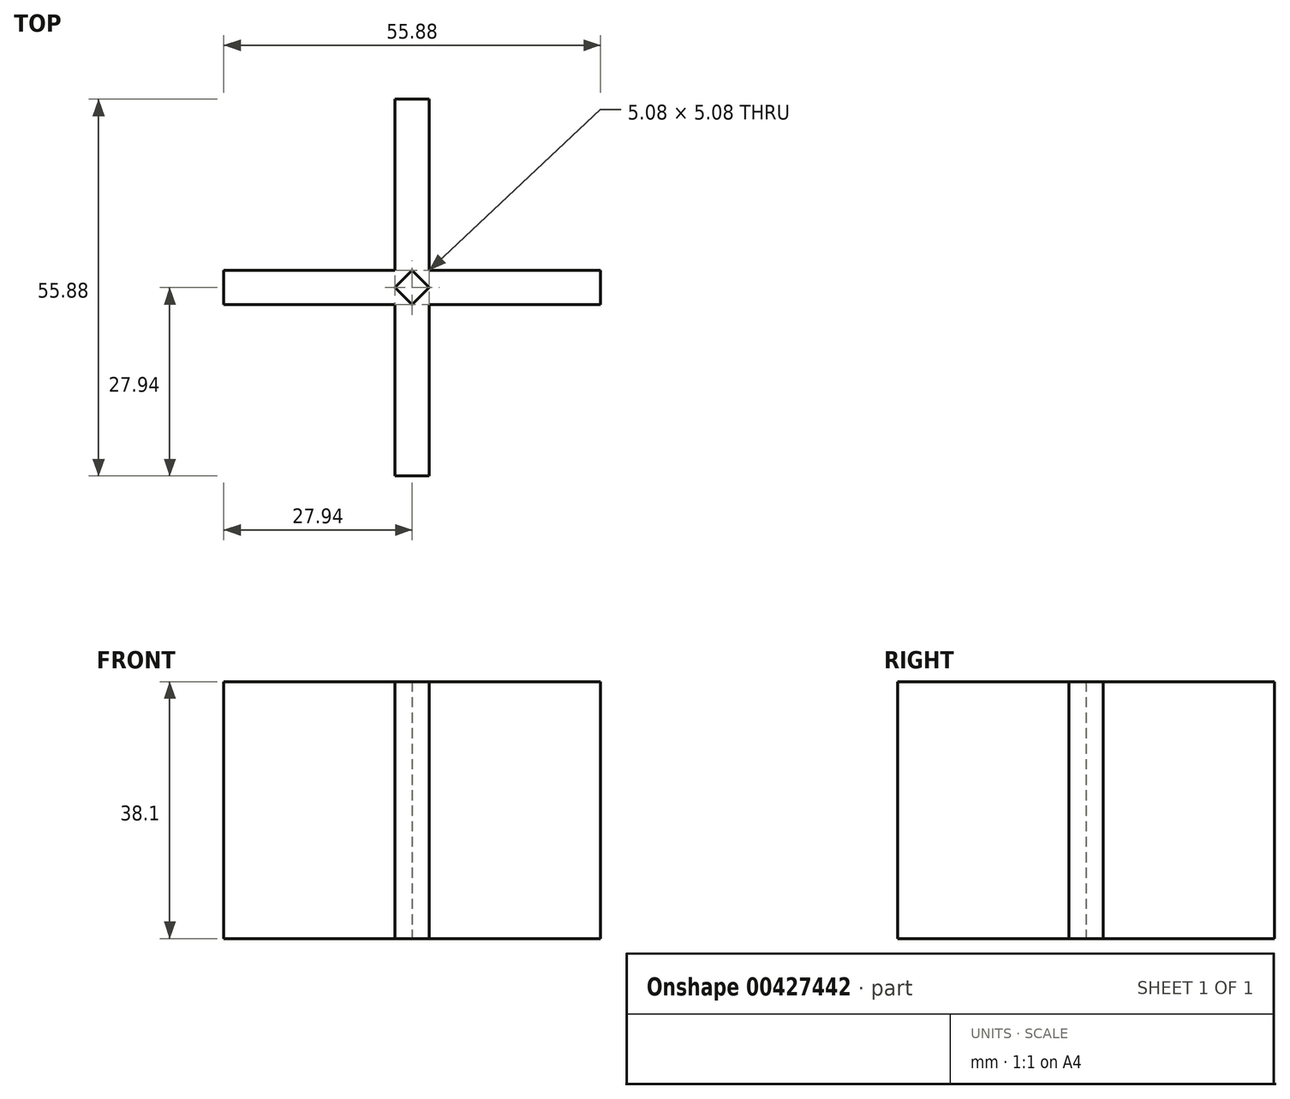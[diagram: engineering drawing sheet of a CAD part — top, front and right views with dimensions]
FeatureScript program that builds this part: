
annotation { "Feature Type Name" : "Feature", "Feature Type Description" : "" }
export const myFeature = defineFeature(function(context is Context, id is Id, definition is map)
    precondition{}
    {
        {
            var Q0;
            Q0=qCreatedBy(makeId("Top.planeOp"),FACE);
            var sketch = newSketch(context, id + "F0", { "sketchPlane" : qUnion([Q0])});
            skLineSegment(sketch, "E0", {"start": v(0, 0) * mm, "end": v(0, 25.4) * mm});
            skLineSegment(sketch, "E1", {"start": v(0, 25.4) * mm, "end": v(5.08, 25.4) * mm});
            skLineSegment(sketch, "E2", {"start": v(5.08, -30.48) * mm, "end": v(0, -30.48) * mm});
            skLineSegment(sketch, "E3", {"start": v(0, -30.48) * mm, "end": v(0, -5.08) * mm});
            skLineSegment(sketch, "E4", {"start": v(0, -5.08) * mm, "end": v(-25.4, -5.08) * mm});
            skLineSegment(sketch, "E5", {"start": v(-25.4, -5.08) * mm, "end": v(-25.4, 0) * mm});
            skLineSegment(sketch, "E6", {"start": v(-25.4, 0) * mm, "end": v(0, 0) * mm});
            skLineSegment(sketch, "E7", {"start": v(5.08, 25.4) * mm, "end": v(5.08, 0) * mm});
            skLineSegment(sketch, "E8", {"start": v(5.08, 0) * mm, "end": v(30.48, 0) * mm});
            skLineSegment(sketch, "E9", {"start": v(5.08, -30.48) * mm, "end": v(5.08, -5.08) * mm});
            skLineSegment(sketch, "E10", {"start": v(5.08, -5.08) * mm, "end": v(30.47, -5.08) * mm});
            skLineSegment(sketch, "E11", {"start": v(30.47, -5.08) * mm, "end": v(30.48, 0) * mm});
            skLineSegment(sketch, "E12", {"start": v(2.54, 0) * mm, "end": v(0, -2.54) * mm});
            skLineSegment(sketch, "E13", {"start": v(0, -2.54) * mm, "end": v(2.54, -5.08) * mm});
            skLineSegment(sketch, "E14", {"start": v(2.54, -5.08) * mm, "end": v(5.08, -2.54) * mm});
            skLineSegment(sketch, "E15", {"start": v(5.08, -2.54) * mm, "end": v(2.54, 0) * mm});
            skSolve(sketch);
        }
        {
            var Q0;
            Q0=makeQuery(id+"F0.imprint","IMPRINT",FACE,{"disambiguationData":[TD([[makeQuery(id+"F0.imprint","IMPRINT",EDGE,{"derivedFrom":sQuery(id+"F0.wireOp",EDGE,"E0")}),-1.0]])]});
            extrude(context, id + "F1", {"entities" : qUnion([Q0]), "depth" : 38.1 * mm});
        }
    });
